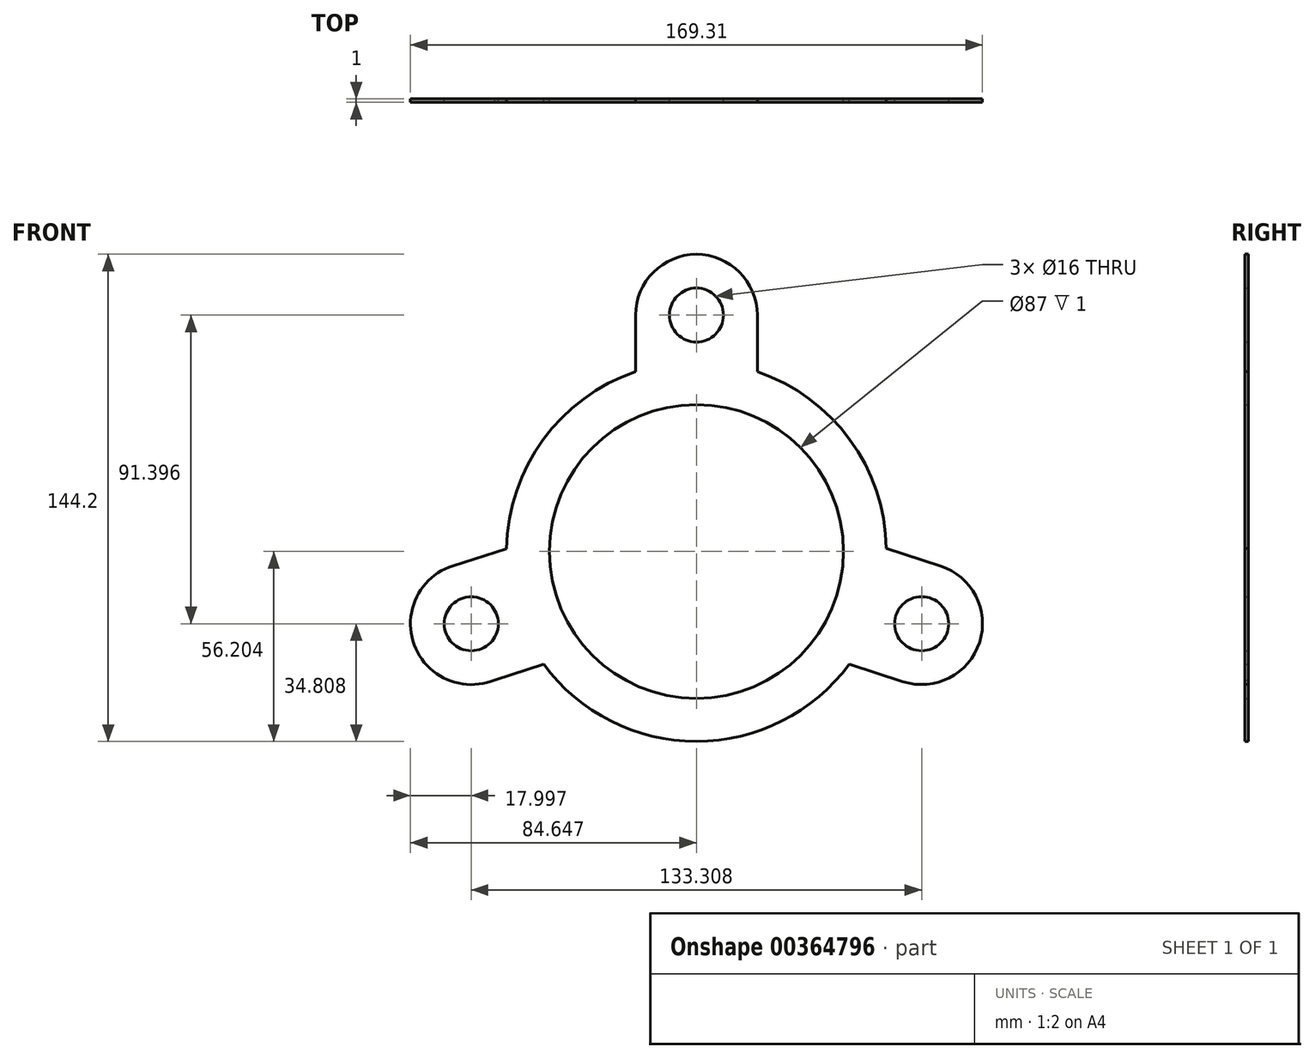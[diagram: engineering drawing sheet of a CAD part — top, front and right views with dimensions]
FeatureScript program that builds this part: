
annotation { "Feature Type Name" : "Feature", "Feature Type Description" : "" }
export const myFeature = defineFeature(function(context is Context, id is Id, definition is map)
    precondition{}
    {
        {
            var Q0;
            Q0=qCreatedBy(makeId("Front.planeOp"),FACE);
            var sketch = newSketch(context, id + "F0", { "sketchPlane" : qUnion([Q0])});
            skCircle(sketch, "E0", {"center": v(0.44, 0.4) * mm, "radius": 56.2 * mm});
            skCircle(sketch, "E1", {"center": v(0.44, 0.4) * mm, "radius": 43.5 * mm});
            skCircle(sketch, "E2", {"center": v(0.44, 70.4) * mm, "radius": 8 * mm});
            skArc(sketch, "E3", {"start": v(18.44, 70.4) * mm, "mid": v(0.44, 88.4) * mm, "end": v(-17.56, 70.4) * mm});
            skLineSegment(sketch, "E4", {"start": v(-17.56, 70.4) * mm, "end": v(-17.56, 49.71) * mm});
            skLineSegment(sketch, "E5", {"start": v(18.44, 70.4) * mm, "end": v(18.44, 49.71) * mm});
            skCircle(sketch, "E6", {"center": v(-66.21, -21) * mm, "radius": 8 * mm});
            skArc(sketch, "E7", {"start": v(-71.71, -3.86) * mm, "mid": v(-83.1, -27.23) * mm, "end": v(-59.27, -37.61) * mm});
            skCircle(sketch, "E8", {"center": v(67.1, -20.97) * mm, "radius": 8 * mm});
            skArc(sketch, "E9", {"start": v(61.6, -38.12) * mm, "mid": v(84.24, -26.47) * mm, "end": v(72.6, -3.83) * mm});
            skLineSegment(sketch, "E10", {"start": v(-71.71, -3.86) * mm, "end": v(-52.02, 2.46) * mm});
            skLineSegment(sketch, "E11", {"start": v(-59.27, -37.61) * mm, "end": v(-41.06, -31.76) * mm});
            skLineSegment(sketch, "E12.0", {"start": v(72.6, -3.83) * mm, "end": v(52.9, 2.48) * mm});
            skLineSegment(sketch, "E13.0", {"start": v(61.6, -38.12) * mm, "end": v(41.9, -31.8) * mm});
            skSolve(sketch);
        }
        {
            var Q0;
            Q0=makeQuery(id+"F0.imprint","IMPRINT",FACE,{"disambiguationData":[TD([[makeQuery(id+"F0.imprint","IMPRINT",EDGE,{"derivedFrom":sQuery(id+"F0.wireOp",EDGE,"E1")}),-1.0]])]});
            var Q1;
            Q1=makeQuery(id+"F0.imprint","IMPRINT",FACE,{"disambiguationData":[TD([[makeQuery(id+"F0.imprint","IMPRINT",EDGE,{"derivedFrom":sQuery(id+"F0.wireOp",EDGE,"E6")}),-1.0]])]});
            var Q2;
            Q2=makeQuery(id+"F0.imprint","IMPRINT",FACE,{"disambiguationData":[TD([[makeQuery(id+"F0.imprint","IMPRINT",EDGE,{"derivedFrom":sQuery(id+"F0.wireOp",EDGE,"E8")}),-1.0]])]});
            var Q3;
            Q3=makeQuery(id+"F0.imprint","IMPRINT",FACE,{"disambiguationData":[TD([[makeQuery(id+"F0.imprint","IMPRINT",EDGE,{"derivedFrom":sQuery(id+"F0.wireOp",EDGE,"E2")}),-1.0]])]});
            extrude(context, id + "F1", {"entities" : qUnion([Q0, Q1, Q2, Q3]), "depth" : 1 * mm, "offsetDistance" : 25 * mm});
        }
    });
